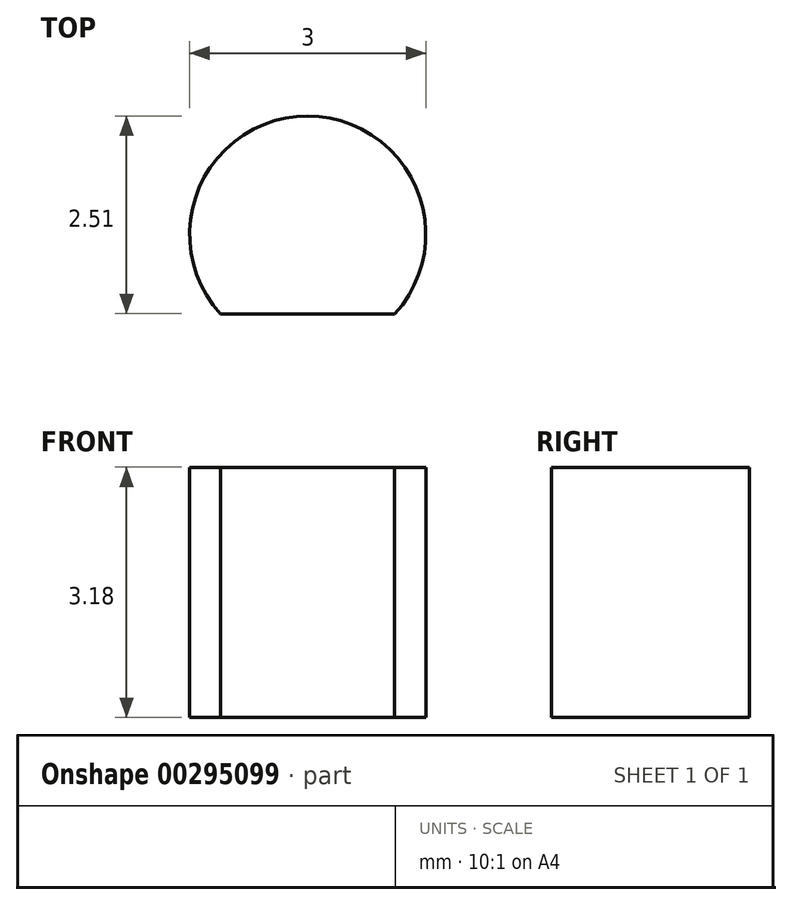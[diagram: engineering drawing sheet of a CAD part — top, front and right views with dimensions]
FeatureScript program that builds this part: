
annotation { "Feature Type Name" : "Feature", "Feature Type Description" : "" }
export const myFeature = defineFeature(function(context is Context, id is Id, definition is map)
    precondition{}
    {
        {
            var Q0;
            Q0=qCreatedBy(makeId("Top.planeOp"),FACE);
            var sketch = newSketch(context, id + "F0", { "sketchPlane" : qUnion([Q0])});
            skCircle(sketch, "E0", {"center": v(0, 7.62) * mm, "radius": 1.59 * mm});
            skCircle(sketch, "E1.1.0", {"center": v(-6.6, -3.8) * mm, "radius": 1.59 * mm});
            skCircle(sketch, "E1.2.0", {"center": v(6.6, -3.81) * mm, "radius": 1.59 * mm});
            skPoint(sketch, "E1.center", {"position": v(0, 0) * mm});
            skCircle(sketch, "E2", {"center": v(0, 0) * mm, "radius": 12.7 * mm});
            skSolve(sketch);
        }
        {
            var Q0;
            Q0=makeQuery(id+"F0.imprint","IMPRINT",FACE,{"disambiguationData":[TD([[makeQuery(id+"F0.imprint","IMPRINT",EDGE,{"derivedFrom":sQuery(id+"F0.wireOp",EDGE,"E0")}),-1.0]])]});
            extrude(context, id + "F1", {"entities" : qUnion([Q0]), "depth" : 3.17 * mm});
        }
        {
            var Q0;
            Q0=makeQuery(id+"F1.opExtrude","CAP_FACE",FACE,{"disambiguationData":[OSD([sQuery(id+"F0.wireOp",EDGE,"E0"),sQuery(id+"F0.wireOp",EDGE,"E1.1.0"),sQuery(id+"F0.wireOp",EDGE,"E1.2.0"),sQuery(id+"F0.wireOp",EDGE,"E2")])],"isStart":false});
            var sketch = newSketch(context, id + "F2", { "sketchPlane" : qUnion([Q0])});
            skArc(sketch, "E3", {"start": v(-1.1, -1.01) * mm, "mid": v(0, 1.5) * mm, "end": v(1.1, -1.01) * mm});
            skLineSegment(sketch, "E4", {"start": v(1.1, -1.01) * mm, "end": v(-1.1, -1.01) * mm});
            skSolve(sketch);
        }
        {
            var Q0;
            Q0=makeQuery(id+"F2.imprint","IMPRINT",FACE,{"disambiguationData":[TD([[makeQuery(id+"F2.imprint","IMPRINT",EDGE,{"derivedFrom":sQuery(id+"F2.wireOp",EDGE,"E3")}),1.0]])]});
            extrude(context, id + "F3", {"entities" : qUnion([Q0]), "operationType" : NewBodyOperationType.INTERSECT, "oppositeDirection" : true, "depth" : 25.4 * mm});
        }
    });
